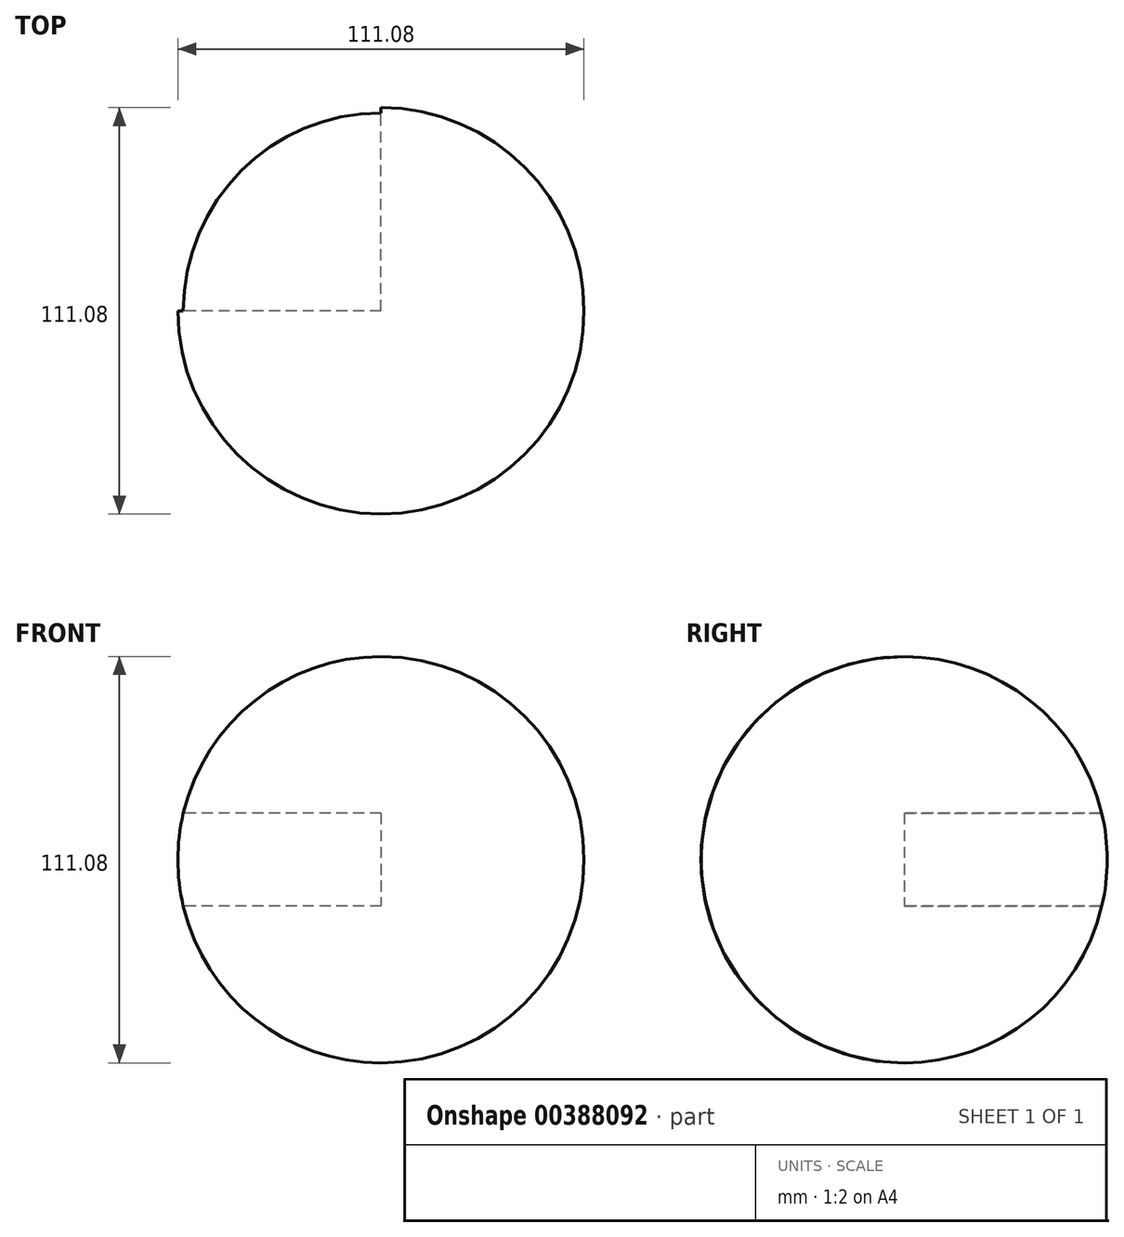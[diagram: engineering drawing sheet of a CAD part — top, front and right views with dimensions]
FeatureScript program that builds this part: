
annotation { "Feature Type Name" : "Feature", "Feature Type Description" : "" }
export const myFeature = defineFeature(function(context is Context, id is Id, definition is map)
    precondition{}
    {
        {
            var Q0;
            Q0=qCreatedBy(makeId("Front.planeOp"),FACE);
            var sketch = newSketch(context, id + "F0", { "sketchPlane" : qUnion([Q0])});
            skArc(sketch, "E0", {"start": v(0, 55.54) * mm, "mid": v(-55.54, 0) * mm, "end": v(0, -55.54) * mm});
            skLineSegment(sketch, "E1", {"start": v(0, 0) * mm, "end": v(0, 55.54) * mm, "construction": true});
            skLineSegment(sketch, "E2", {"start": v(0, 55.54) * mm, "end": v(0, -55.54) * mm});
            skSolve(sketch);
        }
        {
            var Q0;
            Q0=makeQuery(id+"F0.imprint","IMPRINT",FACE,{"disambiguationData":[TD([[makeQuery(id+"F0.imprint","IMPRINT",EDGE,{"derivedFrom":sQuery(id+"F0.wireOp",EDGE,"E0")}),1.0]])]});
            var Q1;
            Q1=sQuery(id+"F0.wireOp",EDGE,"E0");
            var Q2;
            Q2=sQuery(id+"F0.wireOp",EDGE,"E1");
            revolve(context, id + "F1", {"entities" : qUnion([Q0]), "surfaceEntities" : qUnion([Q1]), "axis" : qUnion([Q2]), "revolveType" : RevolveType.FULL});
        }
        {
            var Q0;
            Q0=qCreatedBy(makeId("Top.planeOp"),FACE);
            var sketch = newSketch(context, id + "F2", { "sketchPlane" : qUnion([Q0])});
            skLineSegment(sketch, "E3.bottom", {"start": v(0, 0) * mm, "end": v(-65.98, 0) * mm});
            skLineSegment(sketch, "E3.top", {"start": v(0, 65.1) * mm, "end": v(-65.98, 65.1) * mm});
            skLineSegment(sketch, "E3.left", {"start": v(0, 0) * mm, "end": v(0, 65.1) * mm});
            skLineSegment(sketch, "E3.right", {"start": v(-65.98, 0) * mm, "end": v(-65.98, 65.1) * mm});
            skSolve(sketch);
        }
        {
            var Q0;
            Q0 = qSketchRegion(id + "F2", true);
            extrude(context, id + "F3", {"entities" : qUnion([Q0]), "operationType" : NewBodyOperationType.REMOVE, "endBound" : BoundingType.SYMMETRIC, "depth" : 25.4 * mm});
        }
    });
